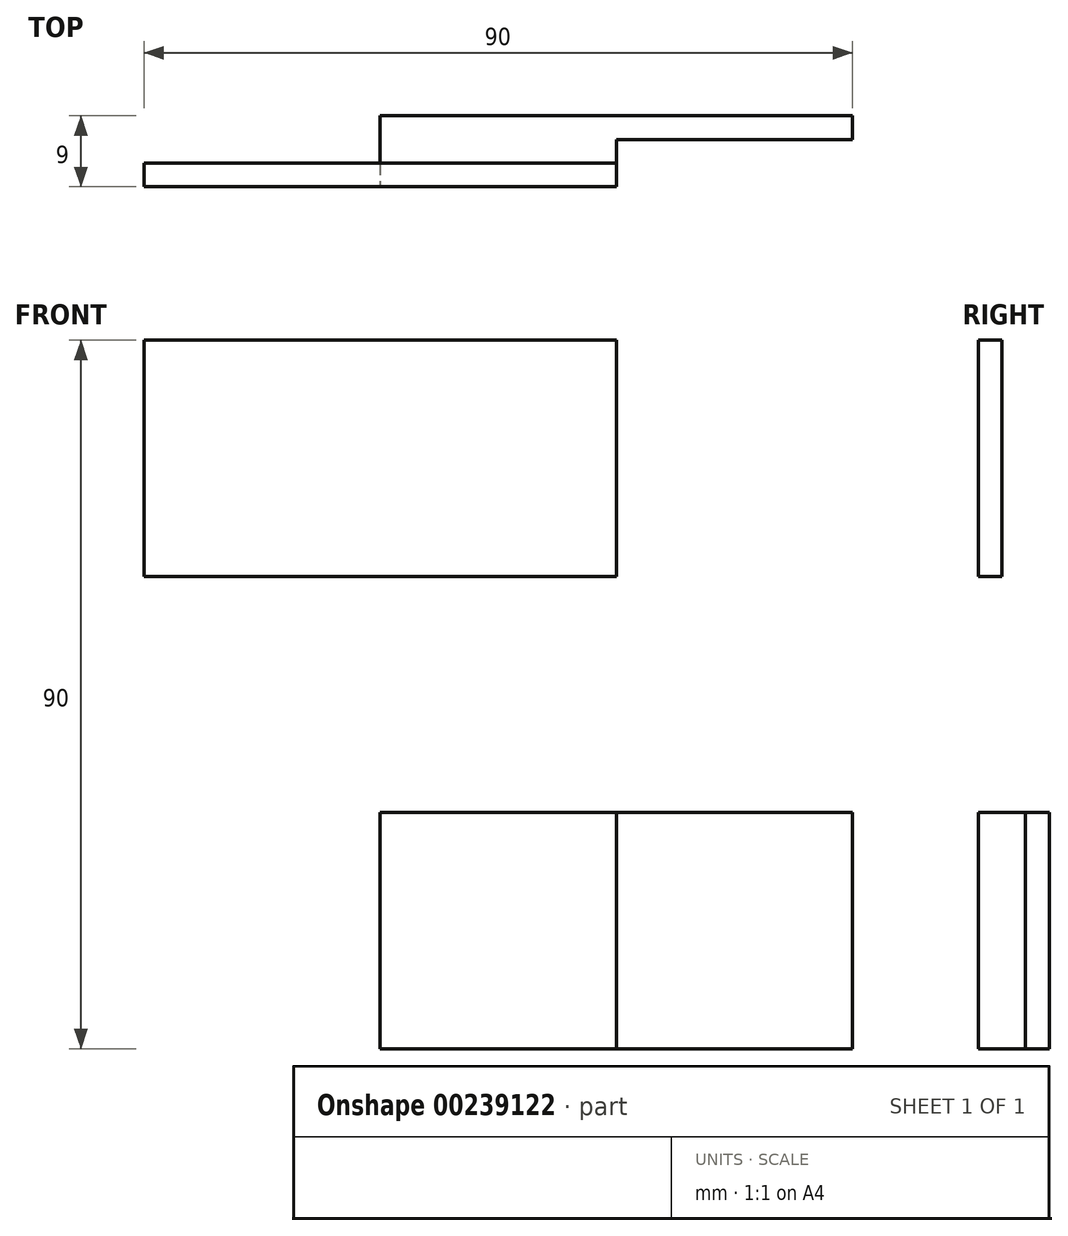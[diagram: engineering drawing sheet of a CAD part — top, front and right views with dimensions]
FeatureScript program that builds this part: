
annotation { "Feature Type Name" : "Feature", "Feature Type Description" : "" }
export const myFeature = defineFeature(function(context is Context, id is Id, definition is map)
    precondition{}
    {
        {
            assignVariable(context, id + "F0", {"name" : "e", "anyValue" : 3});
        }
        {
            var Q0;
            Q0=qCreatedBy(makeId("Front.planeOp"),FACE);
            var sketch = newSketch(context, id + "F1", { "sketchPlane" : qUnion([Q0])});
            skLineSegment(sketch, "E0.bottom", {"start": v(45, 45) * mm, "end": v(-45, 45) * mm});
            skLineSegment(sketch, "E0.top", {"start": v(45, -45) * mm, "end": v(-45, -45) * mm});
            skLineSegment(sketch, "E0.left", {"start": v(45, 45) * mm, "end": v(45, -45) * mm});
            skLineSegment(sketch, "E0.right", {"start": v(-45, 45) * mm, "end": v(-45, -45) * mm});
            skPoint(sketch, "E0.middle", {"position": v(0, 0) * mm});
            skSolve(sketch);
        }
        {
            var Q0;
            Q0=makeQuery(id+"F1.imprint","IMPRINT",FACE,{"disambiguationData":[TD([[makeQuery(id+"F1.imprint","IMPRINT",EDGE,{"derivedFrom":sQuery(id+"F1.wireOp",EDGE,"E0.bottom")}),1.0]])]});
            extrude(context, id + "F2", {"entities" : qUnion([Q0]), "endBound" : BoundingType.SYMMETRIC, "depth" : (3 * getVariable(context, 'e')) * mm});
        }
        {
            var Q0;
            Q0=makeQuery(id+"F2.opExtrude","CAP_FACE",FACE,{"disambiguationData":[OSD([sQuery(id+"F1.wireOp",EDGE,"E0.bottom"),sQuery(id+"F1.wireOp",EDGE,"E0.top"),sQuery(id+"F1.wireOp",EDGE,"E0.left"),sQuery(id+"F1.wireOp",EDGE,"E0.right")])],"isStart":false});
            var sketch = newSketch(context, id + "F3", { "sketchPlane" : qUnion([Q0])});
            skLineSegment(sketch, "E1.bottom", {"start": v(15, 15) * mm, "end": v(-15, 15) * mm});
            skLineSegment(sketch, "E1.top", {"start": v(15, -15) * mm, "end": v(-15, -15) * mm});
            skLineSegment(sketch, "E1.left", {"start": v(15, 15) * mm, "end": v(15, -15) * mm});
            skLineSegment(sketch, "E1.right", {"start": v(-15, 15) * mm, "end": v(-15, -15) * mm});
            skPoint(sketch, "E1.middle", {"position": v(0, 0) * mm});
            skSolve(sketch);
        }
        {
            var Q0;
            Q0 = qSketchRegion(id + "F3", true);
            extrude(context, id + "F4", {"entities" : qUnion([Q0]), "operationType" : NewBodyOperationType.REMOVE, "endBound" : BoundingType.THROUGH_ALL, "oppositeDirection" : true, "depth" : 25 * mm});
        }
        {
            var Q0;
            Q0=makeQuery(id+"F2.opExtrude","CAP_FACE",FACE,{"disambiguationData":[OSD([sQuery(id+"F1.wireOp",EDGE,"E0.bottom"),sQuery(id+"F1.wireOp",EDGE,"E0.top"),sQuery(id+"F1.wireOp",EDGE,"E0.left"),sQuery(id+"F1.wireOp",EDGE,"E0.right")])],"isStart":false});
            var sketch = newSketch(context, id + "F5", { "sketchPlane" : qUnion([Q0])});
            skLineSegment(sketch, "E2.bottom", {"start": v(15, -15) * mm, "end": v(45, -15) * mm});
            skLineSegment(sketch, "E2.top", {"start": v(15, 45) * mm, "end": v(45, 45) * mm});
            skLineSegment(sketch, "E2.left", {"start": v(15, -15) * mm, "end": v(15, 45) * mm});
            skLineSegment(sketch, "E2.right", {"start": v(45, -15) * mm, "end": v(45, 45) * mm});
            skSolve(sketch);
        }
        {
            var Q0;
            Q0 = qSketchRegion(id + "F5", true);
            extrude(context, id + "F6", {"entities" : qUnion([Q0]), "operationType" : NewBodyOperationType.REMOVE, "endBound" : BoundingType.THROUGH_ALL, "oppositeDirection" : true, "depth" : 25 * mm});
        }
        {
            var Q0;
            Q0=makeQuery(id+"F2.opExtrude","CAP_FACE",FACE,{"disambiguationData":[OSD([sQuery(id+"F1.wireOp",EDGE,"E0.bottom"),sQuery(id+"F1.wireOp",EDGE,"E0.top"),sQuery(id+"F1.wireOp",EDGE,"E0.left"),sQuery(id+"F1.wireOp",EDGE,"E0.right")])],"isStart":false});
            var sketch = newSketch(context, id + "F7", { "sketchPlane" : qUnion([Q0])});
            skLineSegment(sketch, "E3.bottom", {"start": v(45, -15) * mm, "end": v(15, -15) * mm});
            skLineSegment(sketch, "E3.top", {"start": v(45, -45) * mm, "end": v(15, -45) * mm});
            skLineSegment(sketch, "E3.left", {"start": v(45, -15) * mm, "end": v(45, -45) * mm});
            skLineSegment(sketch, "E3.right", {"start": v(15, -15) * mm, "end": v(15, -45) * mm});
            skSolve(sketch);
        }
        {
            var Q0;
            Q0 = qSketchRegion(id + "F7", true);
            extrude(context, id + "F8", {"entities" : qUnion([Q0]), "operationType" : NewBodyOperationType.REMOVE, "oppositeDirection" : true, "depth" : (2 * getVariable(context, 'e')) * mm});
        }
        {
            var Q0;
            Q0=makeQuery(id+"F2.opExtrude","CAP_FACE",FACE,{"disambiguationData":[OSD([sQuery(id+"F1.wireOp",EDGE,"E0.bottom"),sQuery(id+"F1.wireOp",EDGE,"E0.top"),sQuery(id+"F1.wireOp",EDGE,"E0.left"),sQuery(id+"F1.wireOp",EDGE,"E0.right")])],"isStart":true});
            var sketch = newSketch(context, id + "F9", { "sketchPlane" : qUnion([Q0])});
            skLineSegment(sketch, "E4.bottom", {"start": v(-15, 15) * mm, "end": v(45, 15) * mm});
            skLineSegment(sketch, "E4.top", {"start": v(-15, 45) * mm, "end": v(45, 45) * mm});
            skLineSegment(sketch, "E4.left", {"start": v(-15, 15) * mm, "end": v(-15, 45) * mm});
            skLineSegment(sketch, "E4.right", {"start": v(45, 15) * mm, "end": v(45, 45) * mm});
            skSolve(sketch);
        }
        {
            var Q0;
            Q0 = qSketchRegion(id + "F9", true);
            extrude(context, id + "F10", {"entities" : qUnion([Q0]), "operationType" : NewBodyOperationType.REMOVE, "oppositeDirection" : true, "depth" : (2 * getVariable(context, 'e')) * mm});
        }
        {
            var Q0;
            Q0=makeQuery(id+"F10.boolean.opBoolean","COPY",FACE,{"derivedFrom":makeQuery(id+"F10.opExtrude","SWEPT_FACE",FACE,{"disambiguationData":[OSD([sQuery(id+"F9.wireOp",EDGE,"E4.bottom")])]})});
            var sketch = newSketch(context, id + "F11", { "sketchPlane" : qUnion([Q0])});
            skLineSegment(sketch, "E5.bottom", {"start": v(-45, -15) * mm, "end": v(-15, -15) * mm});
            skLineSegment(sketch, "E5.top", {"start": v(-45, 45) * mm, "end": v(-15, 45) * mm});
            skLineSegment(sketch, "E5.left", {"start": v(-45, -15) * mm, "end": v(-45, 45) * mm});
            skLineSegment(sketch, "E5.right", {"start": v(-15, -15) * mm, "end": v(-15, 45) * mm});
            skSolve(sketch);
        }
        {
            var Q0;
            Q0 = qSketchRegion(id + "F11", true);
            extrude(context, id + "F12", {"entities" : qUnion([Q0]), "operationType" : NewBodyOperationType.REMOVE, "endBound" : BoundingType.THROUGH_ALL, "oppositeDirection" : true, "depth" : 25 * mm});
        }
    });
